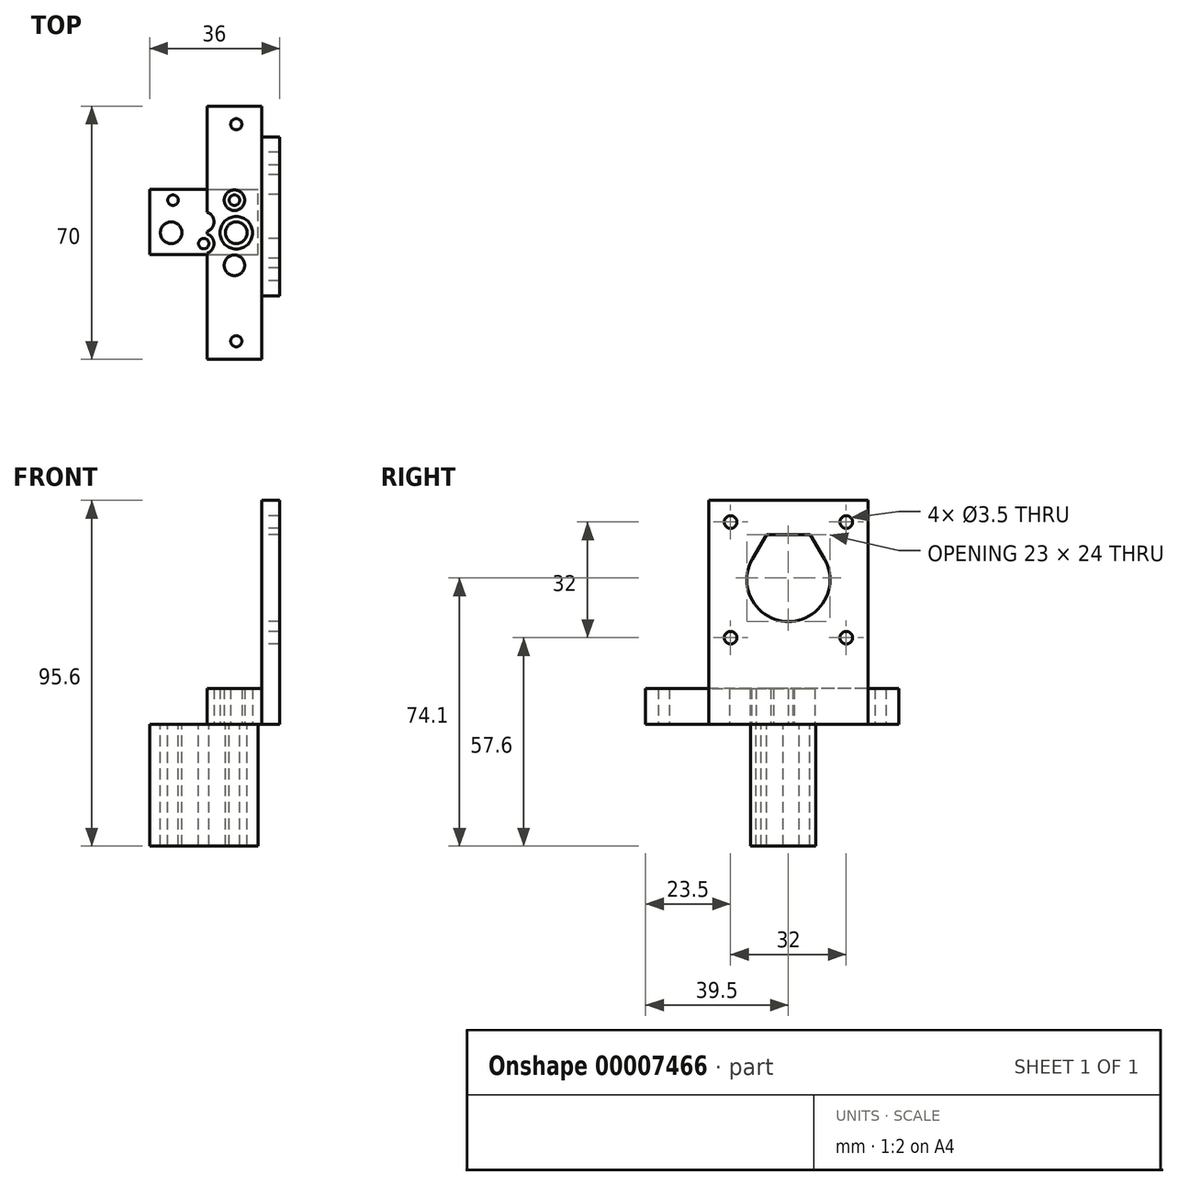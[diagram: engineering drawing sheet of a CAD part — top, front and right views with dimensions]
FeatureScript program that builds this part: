
annotation { "Feature Type Name" : "Feature", "Feature Type Description" : "" }
export const myFeature = defineFeature(function(context is Context, id is Id, definition is map)
    precondition{}
    {
        {
            var Q0;
            Q0=qCreatedBy(makeId("Top.planeOp"),FACE);
            var sketch = newSketch(context, id + "F0", { "sketchPlane" : qUnion([Q0])});
            skLineSegment(sketch, "E0.bottom", {"start": v(0, 0) * mm, "end": v(30, 0) * mm});
            skLineSegment(sketch, "E0.top", {"start": v(0, 18) * mm, "end": v(30, 18) * mm});
            skLineSegment(sketch, "E0.left", {"start": v(0, 0) * mm, "end": v(0, 18) * mm});
            skLineSegment(sketch, "E0.right", {"start": v(30, 0) * mm, "end": v(30, 18) * mm});
            skCircle(sketch, "E1", {"center": v(6, 6) * mm, "radius": 3 * mm});
            skCircle(sketch, "E2", {"center": v(24, 6) * mm, "radius": 3 * mm});
            skCircle(sketch, "E3", {"center": v(6.5, 15) * mm, "radius": 1.45 * mm});
            skCircle(sketch, "E4", {"center": v(23.5, 15) * mm, "radius": 1.45 * mm});
            skCircle(sketch, "E5", {"center": v(15, 3) * mm, "radius": 1.45 * mm});
            skSolve(sketch);
        }
        {
            var Q0;
            Q0=makeQuery(id+"F0.imprint","IMPRINT",FACE,{"disambiguationData":[TD([[makeQuery(id+"F0.imprint","IMPRINT",EDGE,{"derivedFrom":sQuery(id+"F0.wireOp",EDGE,"E0.bottom")}),1.0]])]});
            extrude(context, id + "F1", {"entities" : qUnion([Q0]), "oppositeDirection" : true, "depth" : 33.6 * mm, "offsetDistance" : 25 * mm});
        }
        {
            var Q0;
            Q0=qCreatedBy(makeId("Top.planeOp"),FACE);
            var sketch = newSketch(context, id + "F2", { "sketchPlane" : qUnion([Q0])});
            skCircle(sketch, "E6.0", {"center": v(15, 3) * mm, "radius": 1.45 * mm});
            skCircle(sketch, "E7.0", {"center": v(23.5, 15) * mm, "radius": 1.45 * mm});
            skCircle(sketch, "E8", {"center": v(23.5, 15) * mm, "radius": 2.85 * mm});
            skLineSegment(sketch, "E9", {"start": v(15, 3) * mm, "end": v(15, 26.4) * mm, "construction": true});
            skCircle(sketch, "E10.0", {"center": v(24, 6) * mm, "radius": 3 * mm});
            skCircle(sketch, "E11", {"center": v(24, 6) * mm, "radius": 4.5 * mm});
            skLineSegment(sketch, "E12", {"start": v(24, 6) * mm, "end": v(15, 6) * mm, "construction": true});
            skCircle(sketch, "E13.MirrorC", {"center": v(23.5, -3) * mm, "radius": 2.85 * mm});
            skLineSegment(sketch, "E14", {"start": v(24, 6) * mm, "end": v(31, 6) * mm, "construction": true});
            skLineSegment(sketch, "E15", {"start": v(31, 6) * mm, "end": v(31, 41) * mm});
            skLineSegment(sketch, "E16", {"start": v(31, 41) * mm, "end": v(16, 41) * mm});
            skLineSegment(sketch, "E17", {"start": v(16, 41) * mm, "end": v(16, 6) * mm});
            skCircle(sketch, "E18", {"center": v(24, 36) * mm, "radius": 1.55 * mm});
            skLineSegment(sketch, "E19.MirrorCS", {"start": v(31, 6) * mm, "end": v(31, -29) * mm});
            skLineSegment(sketch, "E20.MirrorCS", {"start": v(16, -29) * mm, "end": v(16, 6) * mm});
            skLineSegment(sketch, "E21.MirrorCS", {"start": v(31, -29) * mm, "end": v(16, -29) * mm});
            skCircle(sketch, "E22.MirrorC", {"center": v(24, -24) * mm, "radius": 1.55 * mm});
            skCircle(sketch, "E23", {"center": v(15, 3) * mm, "radius": 2.85 * mm});
            skCircle(sketch, "E24.MirrorC", {"center": v(15, 9) * mm, "radius": 2.85 * mm});
            skLineSegment(sketch, "E25", {"start": v(36, 10.5) * mm, "end": v(36, 32.5) * mm});
            skLineSegment(sketch, "E26", {"start": v(36, 32.5) * mm, "end": v(31, 32.5) * mm});
            skLineSegment(sketch, "E27", {"start": v(31, 10.5) * mm, "end": v(36, 10.5) * mm, "construction": true});
            skLineSegment(sketch, "E28.MirrorCS", {"start": v(36, 10.5) * mm, "end": v(36, -11.5) * mm});
            skLineSegment(sketch, "E29.MirrorCS", {"start": v(36, -11.5) * mm, "end": v(31, -11.5) * mm});
            skSolve(sketch);
        }
        {
            var Q0;
            Q0=makeQuery(id+"F2.imprint","IMPRINT",FACE,{"disambiguationData":[TD([[makeQuery(id+"F2.imprint","IMPRINT",EDGE,{"derivedFrom":sQuery(id+"F2.wireOp",EDGE,"E8")}),-1.0]])]});
            extrude(context, id + "F3", {"entities" : qUnion([Q0]), "depth" : 10 * mm, "offsetDistance" : 25 * mm});
        }
        {
            var Q0;
            Q0=makeQuery(id+"F2.imprint","IMPRINT",FACE,{"disambiguationData":[TD([[makeQuery(id+"F2.imprint","IMPRINT",EDGE,{"derivedFrom":sQuery(id+"F2.wireOp",EDGE,"E15")}),-1.0]])]});
            extrude(context, id + "F4", {"entities" : qUnion([Q0]), "operationType" : NewBodyOperationType.ADD, "depth" : 62 * mm, "offsetDistance" : 25 * mm});
        }
        {
            var Q0;
            Q0=makeQuery(id+"F4.opExtrude","SWEPT_FACE",FACE,{"disambiguationData":[OSD([sQuery(id+"F2.wireOp",EDGE,"E15"),sQuery(id+"F2.wireOp",EDGE,"E19.MirrorCS")])]});
            var sketch = newSketch(context, id + "F5", { "sketchPlane" : qUnion([Q0])});
            skCircle(sketch, "E30", {"center": v(-10.5, 40) * mm, "radius": 11.5 * mm});
            skLineSegment(sketch, "E31.bottom", {"start": v(-26.5, 24) * mm, "end": v(5.5, 24) * mm, "construction": true});
            skLineSegment(sketch, "E31.top", {"start": v(-26.5, 56) * mm, "end": v(5.5, 56) * mm, "construction": true});
            skLineSegment(sketch, "E31.left", {"start": v(-26.5, 24) * mm, "end": v(-26.5, 56) * mm, "construction": true});
            skLineSegment(sketch, "E31.right", {"start": v(5.5, 24) * mm, "end": v(5.5, 56) * mm, "construction": true});
            skCircle(sketch, "E32", {"center": v(5.5, 56) * mm, "radius": 1.75 * mm});
            skCircle(sketch, "E33", {"center": v(5.5, 24) * mm, "radius": 1.75 * mm});
            skCircle(sketch, "E34", {"center": v(-26.5, 24) * mm, "radius": 1.75 * mm});
            skCircle(sketch, "E35", {"center": v(-26.5, 56) * mm, "radius": 1.75 * mm});
            skLineSegment(sketch, "E36", {"start": v(-20.46, 45.75) * mm, "end": v(-16.56, 52.5) * mm});
            skLineSegment(sketch, "E37", {"start": v(-16.56, 52.5) * mm, "end": v(-4.44, 52.5) * mm});
            skLineSegment(sketch, "E38", {"start": v(-4.44, 52.5) * mm, "end": v(-0.54, 45.75) * mm});
            skLineSegment(sketch, "E39", {"start": v(-10.5, 40) * mm, "end": v(-10.5, 51.5) * mm, "construction": true});
            skPoint(sketch, "E40", {"position": v(-10.5, 10) * mm});
            skLineSegment(sketch, "E41", {"start": v(-10.5, 40) * mm, "end": v(-10.5, 10) * mm, "construction": true});
            skPoint(sketch, "E42.0", {"position": v(-6, 0) * mm});
            skSolve(sketch);
        }
        {
            var Q0;
            Q0 = qSketchRegion(id + "F5", true);
            extrude(context, id + "F6", {"entities" : qUnion([Q0]), "operationType" : NewBodyOperationType.REMOVE, "oppositeDirection" : true, "depth" : 25 * mm, "offsetDistance" : 25 * mm});
        }
    });
